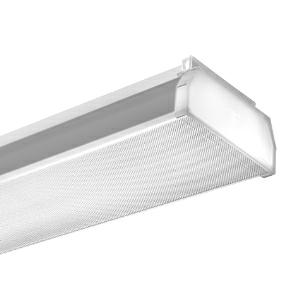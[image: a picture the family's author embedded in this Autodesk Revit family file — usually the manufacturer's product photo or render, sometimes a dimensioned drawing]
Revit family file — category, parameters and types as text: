
# Revit family: 3f_filippi_-_zero_3f_as_3f_filippi_-_1886_-_03f_42w-840_as_l1787
name_source: partatom
category: Lighting Fixtures
units: mm (PartAtom-declared; Revit-internal decimal feet)

## family parameters
Cut with Voids When Loaded = No
Host = Face
Light Source = No
Part Type = Normal
Room Calculation Point = No
Round Connector Dimension = Use Diameter
Shared = No

## types (1)
- 3F Filippi - Zero 3F AS (1 x LED, 5780 lm, 46 W, 4000 K)
    Apparent Load = 46 VA
    Approval mark = CE
    CIE Flux Codes = 51 80 93 88 100
    Color Rendering = 80
    Color Temperature = 4000 K
    Control Gear = Electronic ballast
    Default Elevation = 1800 mm
    Description = ILLUMINOTECHNICAL
Luminous efficiency 100% (DLOR 88%, ULOR 12%).
Initial luminous flux of the luminaire 5780 lm.
Asymmetric distribution.
Beam angle: 99° - 100°.
Luminous efficacy 126 lm/W.
Lifetime (L93/B10): 30000 h. (tq+25°C)
Lifetime (L90/B10): 50000 h. (tq+25°C)
Lifetime (L85/B10): 80000 h. (tq+25°C)
Lifetime (L80/B10): 100000 h. (tq+25°C)
Sudden decreased luminous flux after 50000 hours: 0% (C0).
Photobiological safety in compliance with IEC/TR 62778: RG0 risk exempt, (IEC 62471).
In compliance with IEC/EN 62722-2-1 - IEC/EN 62717 standards.

SOURCE
Linear LED module 42W/840.
Energy efficiency class (UE 2019/2020 - UE 2019/2015): D.
CIE 13.3 Colour rendering index: CRI >80 (R9 <50%).
IES TM-30 Fidelity Index: Rf = 84 Rg = 95.
CCT nominal colour temperature 4000 K.
Colour initial tolerance (MacAdam): SDCM 3.

MECHANICAL
Housing in hot-galvanised steel, painted in white polyester.
Diffuser with differentiated geometry, made of transparent methacrylate (PMMA) with microprismatic finish, anti-glare on the flat part and opal on the side.
Anti-glare opal methacrylate (PMMA) filter for brightness uniformity.
Lighting end caps in methacrylate (PMMA) opal.
Internal recuperator in white painted steel.
Luminaire with limited surface temperature. - D - (EN 60598-2-24)
Dimensions: 1787x119 mm, height 64 mm. Weight 5.35 kg.
IP40 protection degree.
Mechanical strength to impacts IK06 (1 joule).
Glow-wire test resistance 650°C.

ELECTRICAL
Halogen Free electronic wiring 230V-50/60Hz, power factor 0.95, THD <25%, constant output current, SELV, class I, 1 driver.
Power of the luminaire 46 W.
ENEC - CE.
SAFE FLICKER: PstLM=<1 and SVM=<0.4 (IEC TR 61547-1 and IEC TR 63158), to ensure a more comfortable and safe light.
Luminaire compliant with EN 60598-2-22 for power supply from a centralised emergency system CPSS (Central Power Supply System), not incorporated in the luminaire - high risk areas excluded. The default power and flux are 100% in AC and 100% in DC.
Ambient temperature from 0°C to +35°C.
Temperature class T6 max 85°C.
Relative humidity UR: <85%.

INSTALLATION
Ceiling / Suspended / Wall.
Thanks to the full compatibility for dimensions and fixing distances, this product becomes the perfect solution for updating existing installations.
All accessories dedicated to this product are available on the Catalog and on our website www.3F-Filippi.com.

APPLICATIONS
Suitable product for food production plants (HACCP), IFS (Food Version 6), BRC (GSFS Food Version 7).
Environments: with VDTs, meeting rooms, offices.
Environments: recreational, transit areas, corridors, schools, stairwells.
Environments where soft diffuse light is required for optimal visual comfort.

WARNING
Luminaire designed for disposal/recycling at end-of-life.
Replaceable (LED only) light source by a professional. Replaceable control gear by a professional.
    Height = 64 mm
    Lamp = 1 x LED
    Lamp Light Flux = 5780 lm
    Lamp Power = 46 W
    Lamp count = 1
    Length = 1787 mm
    Lifetime = 50000 h
    Luminous efficacy = 126 lm/W
    Manufacturer = 3F Filippi
    ModVariant = No
    Model = 3F Filippi - 1886 - 03F 42W-840 AS L1787
    Mounting Place = Ceiling
    Mounting Type = Surface mounted
    Number of Poles = 1
    OnlyDefault = Yes
    Power Factor = 1
    Product Name = 3F Filippi - Zero 3F AS
    Product group = ceiling mounted luminaire
    ProductGroupID = 3
    Protection Class = Protection class I
    Protection Degree = IP 40
    RLX_Detail_Level = 1
    RLX_Emergency_Light_Flux = 0 lm
    RLX_Emergency_Type = 0
    RLX_Emergency_Type_DB = No
    RlxData = <blob elided: 160221 chars, md5=9aeab48f>
    Socket = socket
    Standby Power = 0 W
    System Light Flux = 5780 lm
    System Power = 46 W
    Type Comments = Product without accessories
    Type Image = 3ffilippi_zero_3f_as.jpg
    URL = http://relux.com
    VarID = ---
    Voltage = 0 V
    Weight = 0.00 kg
    Width = 119 mm

## geometry (parser evidence)
native form markers: Blend x4, Sweep x12
no freeform markers — native parametric forms only
